# Revit family: PRD_FrankeWS_ShwrHds_EmergencyShowerhead_FAID0002
name_source: partatom
category: Plumbing Fixtures
revit_build: Autodesk Revit 2018 (Build: 20190510_1515(x64)
units: mm (PartAtom-declared; Revit-internal decimal feet)

## family parameters
Cut with Voids When Loaded = Yes
Host = Face
OmniClass Number = 23.45.05.14.99
OmniClass Title = Other Sanitary Washing Plumbing Fixtures
Part Type = Normal
Room Calculation Point = No
Round Connector Dimension = Use Diameter
Shared = Yes

## types (1)
- FAID0002
    AssetType = Fixed
    BIMObjectName = PRD_AR_ShowerHeads_EmergencyShowerhead_FAID0002
    Category = Pr_40_20_87_76, Shower heads
    Color = green
    Default Elevation = 925 mm  [stored 3.03478 ft]
    Description = Emergency shower head DN 20 with wall bracket and rosette, self-draining, green EPS coated brass (RAL 6032). Complies with EN 15154, Part 1. Volumetric flow rate approx. 65 l/min at 1 bar pressure, volumetric flow rate approx. 110 l/min at 3 bar pressure.
    DiameterNominal = 20  [stored 0.0656168 ft]
    DrainSize = 20 mm  [stored 0.0656168 ft]
    DurationUnit = year
    Features = DN 20 with wall bracket and rosette, self-draining
    Finish = EPS coated
    FittingMaterial = PRD_AR_Brass_EPSCoated_Green
    GrossWeight = 1.00 kg
    HasTray = FALSE
    IfcExportAs = IfcSanitaryTerminalType
    IfcExportType = SHOWER
    InletSize = DN-20-3-4INH
    Manufacturer = KWC Group AG
    ManufacturerName = KWC Group AG
    ManufacturerURL = www.kwc.com
    Material = brass
    Model = FAID0002
    ModelNumber = 2030018821
    ModelReference = FAID0002
    NBSDescription = Shower heads
    NBSReference = 45-35-70/333
    Name = Emergency Showerhead FAID0002
    NetWeight = 0.97 kg
    NominalDepth = 420 mm  [stored 1.37795 ft]
    NominalHeight = 138 mm  [stored 0.452756 ft]
    NominalWidth = 55 mm  [stored 0.180446 ft]
    ProductInformation = https://pim.kwc.com
    ShowerHeadDescription = Emergency shower head
    ShowerType = Individual
    Size = 55 x 138 x 420 mm (W x H x D)
    SpoutProjection = 400.00 mm
    Type = Emergency shower head offsetwall
    TypeOfFitting = Wall installation
    URL = www.kwc.com
    Uniclass2015Code = Pr_40_20_87_76
    Uniclass2015Title = Shower heads
    Uniclass2015Version = Products v1.17
    Version = 1
    VolumeFlowRate = 1.83 l/s at 3 bar
    WarrantyDurationUnit = year

note: [stored X ft] marks values corroborated as IEEE doubles in the binary element streams (Revit-internal decimal feet)

## geometry (parser evidence)
native form markers: Sweep x2
no freeform markers — native parametric forms only
